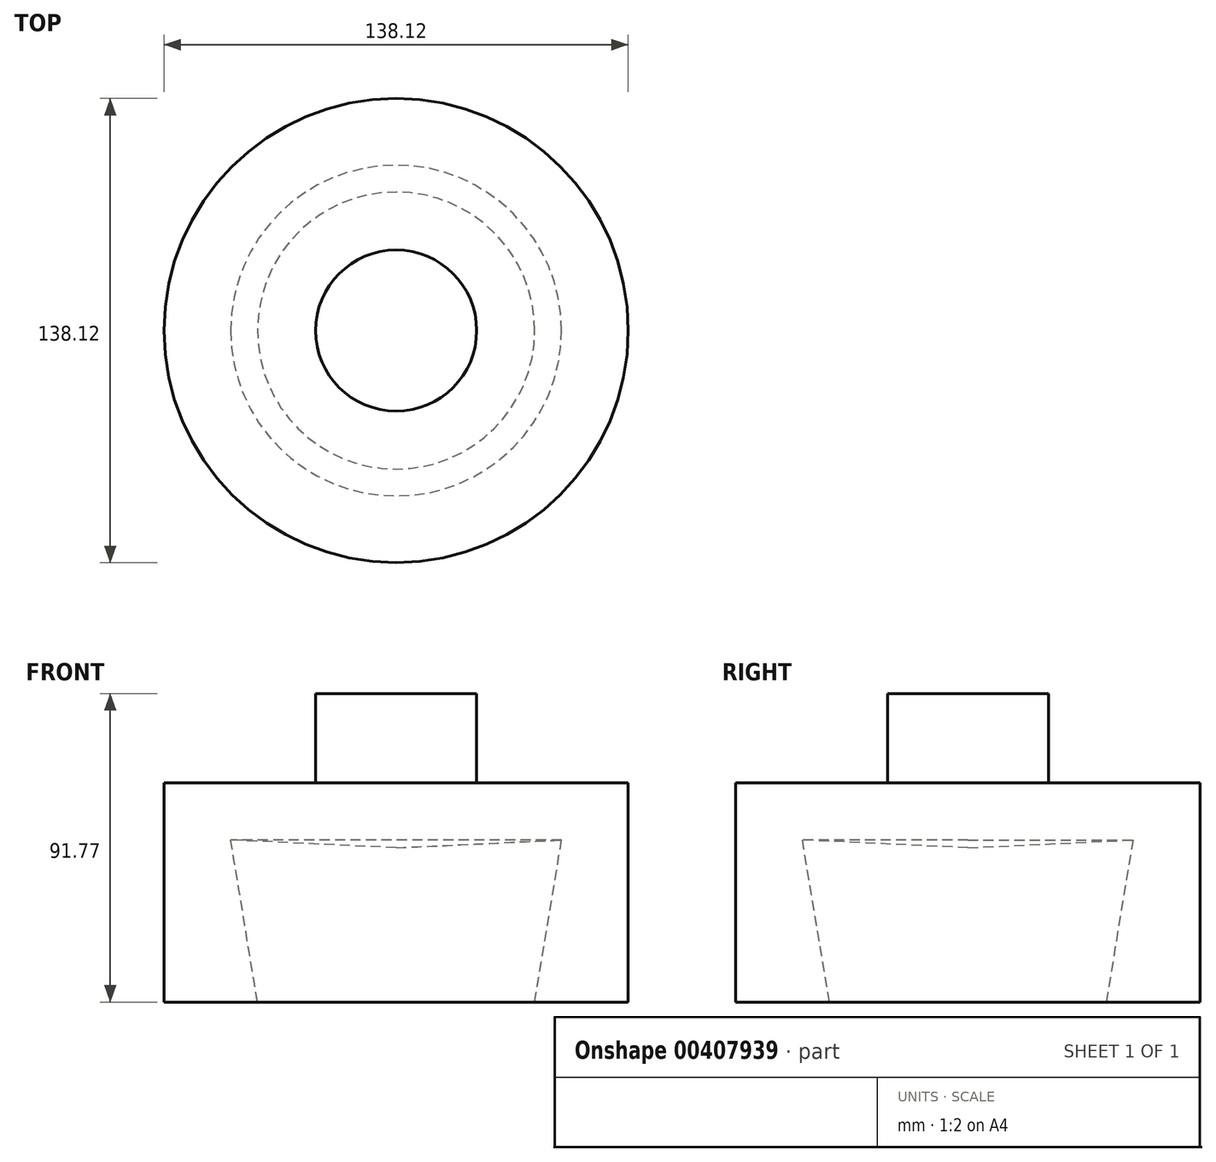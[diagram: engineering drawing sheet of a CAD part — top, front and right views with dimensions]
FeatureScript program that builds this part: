
annotation { "Feature Type Name" : "Feature", "Feature Type Description" : "" }
export const myFeature = defineFeature(function(context is Context, id is Id, definition is map)
    precondition{}
    {
        {
            var Q0;
            Q0=qCreatedBy(makeId("Front.planeOp"),FACE);
            var sketch = newSketch(context, id + "F0", { "sketchPlane" : qUnion([Q0])});
            skLineSegment(sketch, "E0", {"start": v(0, 0) * mm, "end": v(0, 45.87) * mm});
            skLineSegment(sketch, "E1", {"start": v(0, 45.87) * mm, "end": v(23.96, 45.87) * mm});
            skLineSegment(sketch, "E2", {"start": v(23.96, 45.87) * mm, "end": v(23.96, 19.35) * mm});
            skLineSegment(sketch, "E3", {"start": v(23.96, 19.35) * mm, "end": v(69.06, 19.35) * mm});
            skLineSegment(sketch, "E4", {"start": v(69.06, 19.35) * mm, "end": v(69.06, -45.9) * mm});
            skLineSegment(sketch, "E5", {"start": v(69.06, -45.9) * mm, "end": v(41.23, -45.9) * mm});
            skLineSegment(sketch, "E6", {"start": v(41.23, -45.9) * mm, "end": v(49.22, 2.34) * mm});
            skLineSegment(sketch, "E7", {"start": v(49.22, 2.34) * mm, "end": v(0, 0) * mm});
            skSolve(sketch);
        }
        {
            var Q0;
            Q0=makeQuery(id+"F0.imprint","IMPRINT",FACE,{"disambiguationData":[TD([[makeQuery(id+"F0.imprint","IMPRINT",EDGE,{"derivedFrom":sQuery(id+"F0.wireOp",EDGE,"E0")}),-1.0]])]});
            var Q1;
            Q1=sQuery(id+"F0.wireOp",EDGE,"E0");
            revolve(context, id + "F1", {"entities" : qUnion([Q0]), "axis" : qUnion([Q1]), "revolveType" : RevolveType.FULL});
        }
    });
